# Revit family: DC_Rheem_PLM_CPE28_BackToBack
name_source: partatom
category: Plumbing Fixtures
revit_build: Autodesk Revit MEP 2012 (Build: 20110309_2315(x64)
units: mm (PartAtom-declared; Revit-internal decimal feet)

## types (2) — shared parameters
Cold Water Pipe Diameter = 80 mm  [stored 0.262467 ft]
ColdWaterPipeRadius_ANZRS = 40 mm  [stored 0.131234 ft]
GasPipeDiameterD3_ANZRS = 65 mm  [stored 0.213255 ft]
GasPipeRadius_ANZRS = 32.5 mm  [stored 0.106627 ft]
HotWaterOutletDiameterD2_ANZRS = 80 mm  [stored 0.262467 ft]
HotWaterOutletRadius_ANZRS = 40 mm  [stored 0.131234 ft]
HotWaterReturnDiameterD1_ANZRS = 40 mm  [stored 0.131234 ft]
HotWaterReturnRadius_ANZRS = 20 mm  [stored 0.0656168 ft]
Length_ANZRS = 5040 mm  [stored 16.5354 ft]
Manufacturer = Rheem
Materials_ANZRS = Rheem - Antique White
Type Comments = 370L/min @ 50°C rise - Dual 50% capacity pump and controller included
URL = http://www.rheem.com.au
zero-valued in all types: Default Elevation

## per-type parameters (varying)
| type | Model |
| Commpak - Gas Continuous Flow - Outdoor - 5740 MJ/h Natural gas free standing frame - back to back | CPE28NB |
| Commpak - Gas Continuous Flow - Outdoor - 5740 MJ/h Propane gas free standing frame - back to back | CPE28PB |

note: column(s) folded — value = type name in every type: Description

note: [stored X ft] marks values corroborated as IEEE doubles in the binary element streams (Revit-internal decimal feet)

## geometry (parser evidence)
native form markers: Sweep x28
no freeform markers — native parametric forms only
